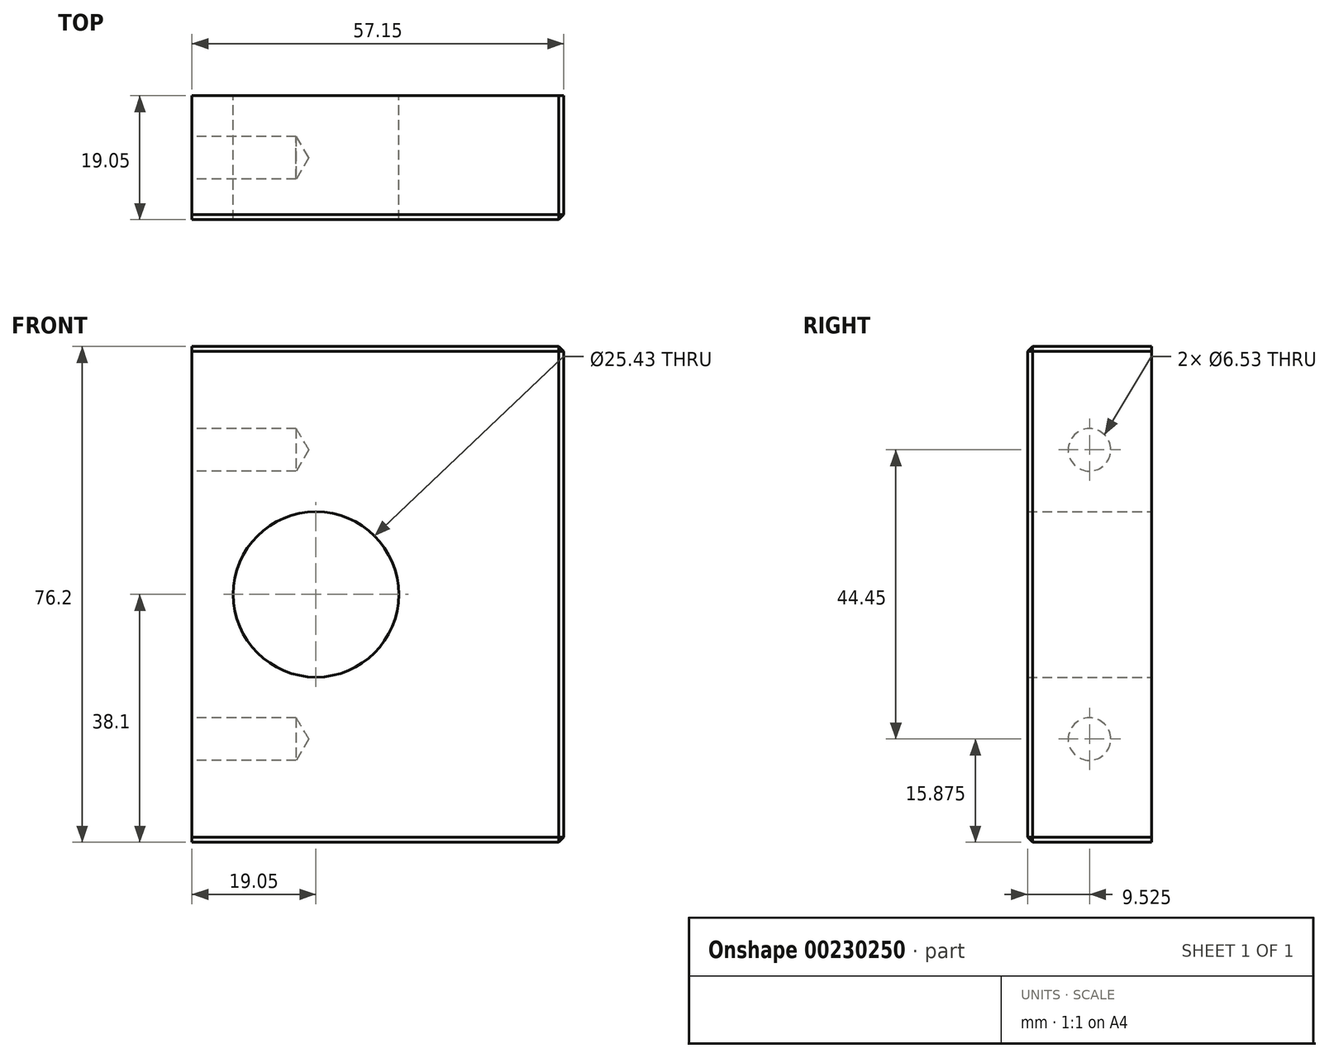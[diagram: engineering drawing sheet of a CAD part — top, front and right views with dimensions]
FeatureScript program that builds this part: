
annotation { "Feature Type Name" : "Feature", "Feature Type Description" : "" }
export const myFeature = defineFeature(function(context is Context, id is Id, definition is map)
    precondition{}
    {
        {
            var Q0;
            Q0=qCreatedBy(makeId("Front.planeOp"),FACE);
            var sketch = newSketch(context, id + "F0", { "sketchPlane" : qUnion([Q0])});
            skLineSegment(sketch, "E0.bottom", {"start": v(0, 0) * mm, "end": v(57.15, 0) * mm});
            skLineSegment(sketch, "E0.top", {"start": v(0, 76.2) * mm, "end": v(57.15, 76.2) * mm});
            skLineSegment(sketch, "E0.left", {"start": v(0, 0) * mm, "end": v(0, 76.2) * mm});
            skLineSegment(sketch, "E0.right", {"start": v(57.15, 0) * mm, "end": v(57.15, 76.2) * mm});
            skCircle(sketch, "E1", {"center": v(19.05, 38.1) * mm, "radius": 12.71 * mm});
            skSolve(sketch);
        }
        {
            var Q0;
            Q0 = qSketchRegion(id + "F0", true);
            extrude(context, id + "F1", {"entities" : qUnion([Q0]), "depth" : 19.05 * mm});
        }
        {
            var Q0;
            Q0=makeQuery(id+"F1.opExtrude","SWEPT_FACE",FACE,{"disambiguationData":[OSD([sQuery(id+"F0.wireOp",EDGE,"E0.left")])]});
            var sketch = newSketch(context, id + "F2", { "sketchPlane" : qUnion([Q0])});
            skLineSegment(sketch, "E2", {"start": v(19.05, 38.1) * mm, "end": v(0, 38.1) * mm});
            skLineSegment(sketch, "E3", {"start": v(9.53, 38.1) * mm, "end": v(9.53, 60.32) * mm});
            skPoint(sketch, "E4", {"position": v(9.53, 60.32) * mm});
            skPoint(sketch, "E5", {"position": v(-94.55, 52.54) * mm});
            skPoint(sketch, "E6.MirrorP", {"position": v(9.53, 15.87) * mm});
            skSolve(sketch);
        }
        {
            var Q0;
            Q0=sQuery(id+"F2.wireOp",VERTEX,"E4");
            var Q1;
            Q1=sQuery(id+"F2.wireOp",VERTEX,"E6.MirrorP");
            var Q2;
            Q2=makeQuery(id+"F1.opExtrude","SWEPT_BODY",BODY,{"disambiguationData":[OSD([sQuery(id+"F0.wireOp",EDGE,"E0.bottom"),sQuery(id+"F0.wireOp",EDGE,"E0.top"),sQuery(id+"F0.wireOp",EDGE,"E0.left"),sQuery(id+"F0.wireOp",EDGE,"E0.right"),sQuery(id+"F0.wireOp",EDGE,"E1")])]});
            hole(context, id + "F3", {"style" : HoleStyle.SIMPLE, "endStyle" : HoleEndStyle.BLIND, "standardTappedOrClearance" : lookupTablePath({ "standard" : "ANSI", "engagement" : "75%", "pitch" : "18 tpi", "size" : "5/16", "type" : "Tapped" }), "standardBlindInLast" : lookupTablePath({ "standard" : "ANSI", "engagement" : "75%", "pitch" : "18 tpi", "size" : "5/16", "type" : "Tapped" }), "holeDiameter" : 6.53 * mm, "holeDepth" : 16 * mm, "locations" : qUnion([Q0, Q1]), "scope" : qUnion([Q2]), "majorDiameter" : 7.94 * mm});
        }
        {
            var Q0;
            Q0=makeQuery(id+"F1.opExtrude","CAP_EDGE",EDGE,{"disambiguationData":[OSD([sQuery(id+"F0.wireOp",EDGE,"E0.right")])],"isStart":false});
            var Q1;
            Q1=makeQuery(id+"F1.opExtrude","CAP_EDGE",EDGE,{"disambiguationData":[OSD([sQuery(id+"F0.wireOp",EDGE,"E0.top")])],"isStart":false});
            var Q2;
            Q2=makeQuery(id+"F1.opExtrude","CAP_EDGE",EDGE,{"disambiguationData":[OSD([sQuery(id+"F0.wireOp",EDGE,"E0.bottom")])],"isStart":false});
            var Q3;
            Q3=makeQuery(id+"F1.opExtrude","SWEPT_EDGE",EDGE,{"disambiguationData":[OSD([sQuery(id+"F0.wireOp",EDGE,"E0.top"),sQuery(id+"F0.wireOp",EDGE,"E0.right")])]});
            var Q4;
            Q4=makeQuery(id+"F1.opExtrude","SWEPT_EDGE",EDGE,{"disambiguationData":[OSD([sQuery(id+"F0.wireOp",EDGE,"E0.bottom"),sQuery(id+"F0.wireOp",EDGE,"E0.right")])]});
            chamfer(context, id + "F4", {"entities" : qUnion([Q0, Q1, Q2, Q3, Q4]), "chamferType" : ChamferType.OFFSET_ANGLE, "width" : 0.76 * mm, "oppositeDirection" : false, "angle" : 45 * degree, "tangentPropagation" : true});
        }
    });
